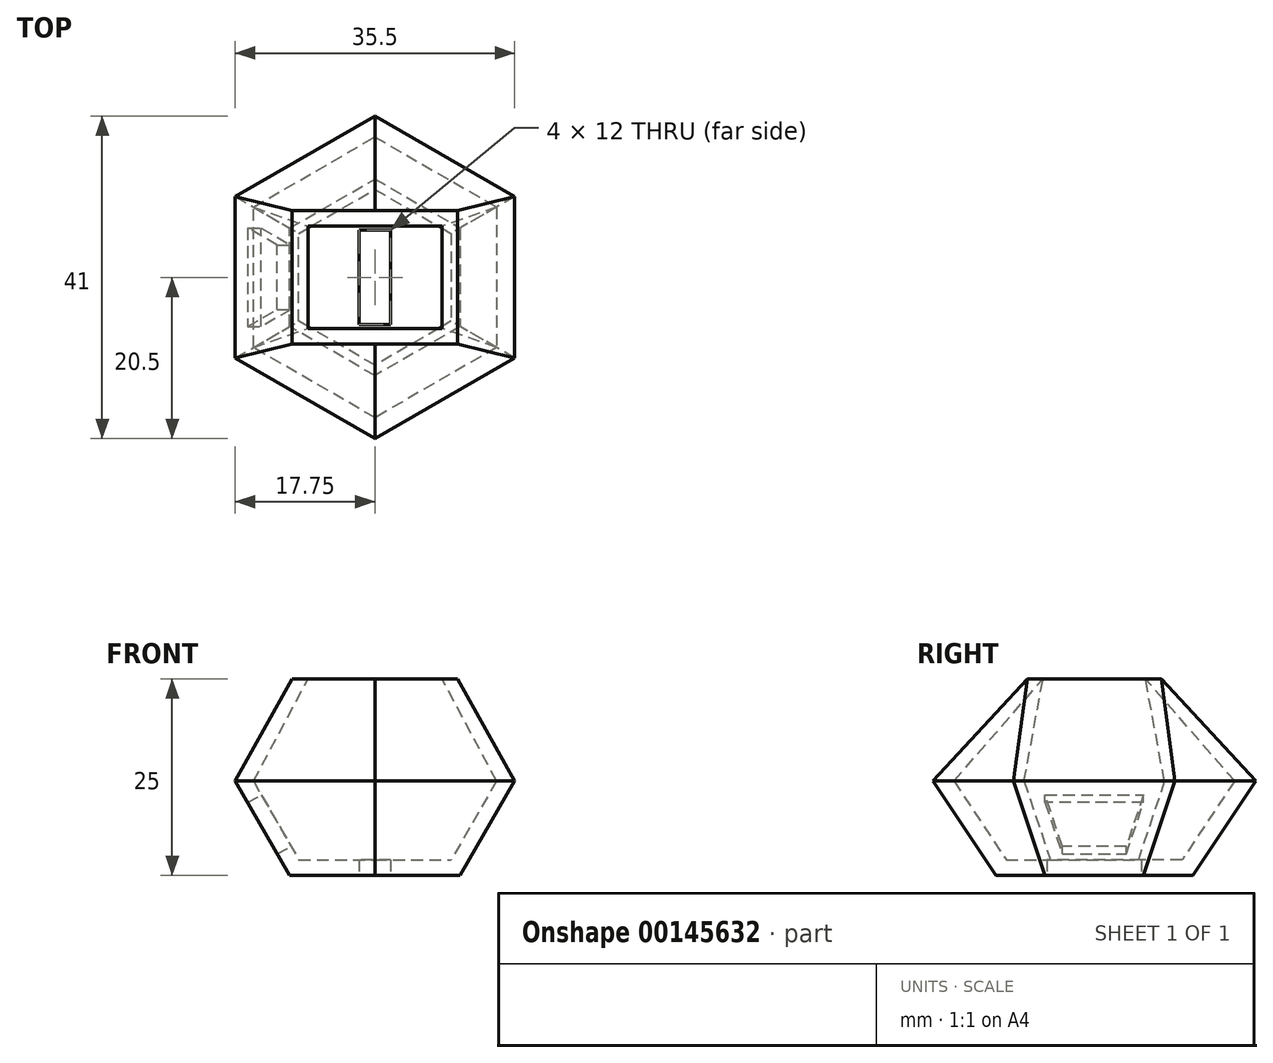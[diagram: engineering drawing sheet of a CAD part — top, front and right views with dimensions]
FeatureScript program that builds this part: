
annotation { "Feature Type Name" : "Feature", "Feature Type Description" : "" }
export const myFeature = defineFeature(function(context is Context, id is Id, definition is map)
    precondition{}
    {
        {
            assignVariable(context, id + "F0", {"name" : "tot_height", "anyValue" : 25});
        }
        {
            assignVariable(context, id + "F1", {"name" : "wall_thick", "anyValue" : 2});
        }
        {
            assignVariable(context, id + "F2", {"name" : "bottom_angle", "anyValue" : 30});
        }
        {
            assignVariable(context, id + "F3", {"name" : "bottom_height", "anyValue" : 12});
        }
        {
            var Q0;
            Q0=qCreatedBy(makeId("Top.planeOp"),FACE);
            var sketch = newSketch(context, id + "F4", { "sketchPlane" : qUnion([Q0])});
            skCircle(sketch, "E0.cCircle", {"center": v(0, 0) * mm, "radius": 12.5 * mm, "construction": true});
            skLineSegment(sketch, "E0.0", {"start": v(0, 12.5) * mm, "end": v(10.83, 6.25) * mm});
            skLineSegment(sketch, "E0.1", {"start": v(10.83, 6.25) * mm, "end": v(10.83, -6.25) * mm});
            skLineSegment(sketch, "E0.2", {"start": v(10.83, -6.25) * mm, "end": v(0, -12.5) * mm});
            skLineSegment(sketch, "E0.3", {"start": v(0, -12.5) * mm, "end": v(-10.83, -6.25) * mm});
            skLineSegment(sketch, "E0.4", {"start": v(-10.83, -6.25) * mm, "end": v(-10.83, 6.25) * mm});
            skLineSegment(sketch, "E0.5", {"start": v(-10.83, 6.25) * mm, "end": v(0, 12.5) * mm});
            skLineSegment(sketch, "E1.bottom", {"start": v(-2, -6) * mm, "end": v(2, -6) * mm});
            skLineSegment(sketch, "E1.top", {"start": v(-2, 6) * mm, "end": v(2, 6) * mm});
            skLineSegment(sketch, "E1.left", {"start": v(-2, -6) * mm, "end": v(-2, 6) * mm});
            skLineSegment(sketch, "E1.right", {"start": v(2, -6) * mm, "end": v(2, 6) * mm});
            skSolve(sketch);
        }
        {
            var Q0;
            Q0 = qSketchRegion(id + "F4", true);
            var Q1;
            Q1=makeQuery(id+"F4.imprint","IMPRINT",FACE,{"disambiguationData":[TD([[makeQuery(id+"F4.imprint","IMPRINT",EDGE,{"derivedFrom":sQuery(id+"F4.wireOp",EDGE,"E1.bottom")}),1.0]])]});
            extrude(context, id + "F5", {"entities" : qUnion([Q0, Q1]), "depth" : (getVariable(context, 'bottom_height')) * mm, "hasDraft" : true, "draftAngle" : (getVariable(context, 'bottom_angle')) * degree});
        }
        {
            var Q0;
            Q0=makeQuery(id+"F5.opExtrude","CAP_FACE",FACE,{"disambiguationData":[OSD([sQuery(id+"F4.wireOp",EDGE,"b764b78a-1ece-4713-94bb-0b7ff5981961.0"),sQuery(id+"F4.wireOp",EDGE,"b764b78a-1ece-4713-94bb-0b7ff5981961.1"),sQuery(id+"F4.wireOp",EDGE,"b764b78a-1ece-4713-94bb-0b7ff5981961.2"),sQuery(id+"F4.wireOp",EDGE,"b764b78a-1ece-4713-94bb-0b7ff5981961.3"),sQuery(id+"F4.wireOp",EDGE,"b764b78a-1ece-4713-94bb-0b7ff5981961.4"),sQuery(id+"F4.wireOp",EDGE,"b764b78a-1ece-4713-94bb-0b7ff5981961.5"),sQuery(id+"F4.wireOp",EDGE,"b764b78a-1ece-4713-94bb-0b7ff5981961.6"),sQuery(id+"F4.wireOp",EDGE,"b764b78a-1ece-4713-94bb-0b7ff5981961.7")])],"isStart":false});
            var Q1;
            Q1=makeQuery(id+"F5.opExtrude","CAP_FACE",FACE,{"disambiguationData":[OSD([sQuery(id+"F4.wireOp",EDGE,"E0.0"),sQuery(id+"F4.wireOp",EDGE,"E0.1"),sQuery(id+"F4.wireOp",EDGE,"E0.2"),sQuery(id+"F4.wireOp",EDGE,"E0.3"),sQuery(id+"F4.wireOp",EDGE,"E0.4"),sQuery(id+"F4.wireOp",EDGE,"E0.5")])],"isStart":false});
            shell(context, id + "F6", {"entities" : qUnion([Q0, Q1]), "thickness" : getVariable(context, 'wall_thick') * mm});
        }
        {
            var Q0;
            Q0=makeQuery(id+"F4.imprint","IMPRINT",FACE,{"disambiguationData":[TD([[makeQuery(id+"F4.imprint","IMPRINT",EDGE,{"derivedFrom":sQuery(id+"F4.wireOp",EDGE,"E1.bottom")}),1.0]])]});
            extrude(context, id + "F7", {"entities" : qUnion([Q0]), "operationType" : NewBodyOperationType.REMOVE, "depth" : 5 * mm});
        }
        {
            var Q0;
            Q0=makeQuery(id+"F6.opShell","OFFSET_FACE",FACE,{"disambiguationData":[OSD([sQuery(id+"F4.wireOp",EDGE,"E0.4")])]});
            var sketch = newSketch(context, id + "F8", { "sketchPlane" : qUnion([Q0])});
            skLineSegment(sketch, "E2", {"start": v(-6.26, 16.11) * mm, "end": v(6.26, 16.11) * mm});
            skLineSegment(sketch, "E3", {"start": v(6.26, 16.11) * mm, "end": v(4.08, 8.57) * mm});
            skLineSegment(sketch, "E4", {"start": v(4.08, 8.57) * mm, "end": v(-4.08, 8.57) * mm});
            skLineSegment(sketch, "E5", {"start": v(-4.08, 8.57) * mm, "end": v(-6.26, 16.11) * mm});
            skSolve(sketch);
        }
        {
            var Q0;
            Q0 = qSketchRegion(id + "F8", true);
            var Q1;
            Q1=makeQuery(id+"F6.opShell","OFFSET_FACE",FACE,{"disambiguationData":[OSD([sQuery(id+"F4.wireOp",EDGE,"b764b78a-1ece-4713-94bb-0b7ff5981961.2")])]});
            extrude(context, id + "F9", {"entities" : qUnion([Q0]), "operationType" : NewBodyOperationType.REMOVE, "oppositeDirection" : true, "endBoundEntityFace" : qUnion([Q1]), "depth" : 10 * mm});
        }
        {
            var Q0;
            Q0=makeQuery(id+"F5.opExtrude","CAP_FACE",FACE,{"disambiguationData":[OSD([sQuery(id+"F4.wireOp",EDGE,"E0.0"),sQuery(id+"F4.wireOp",EDGE,"E0.1"),sQuery(id+"F4.wireOp",EDGE,"E0.2"),sQuery(id+"F4.wireOp",EDGE,"E0.3"),sQuery(id+"F4.wireOp",EDGE,"E0.4"),sQuery(id+"F4.wireOp",EDGE,"E0.5")])],"isStart":false});
            var sketch = newSketch(context, id + "F10", { "sketchPlane" : qUnion([Q0])});
            skLineSegment(sketch, "E6.0", {"start": v(-17.75, 10.25) * mm, "end": v(0, 20.5) * mm});
            skLineSegment(sketch, "E7.0", {"start": v(0, 20.5) * mm, "end": v(17.75, 10.25) * mm});
            skLineSegment(sketch, "E8.0", {"start": v(17.75, 10.25) * mm, "end": v(17.75, -10.25) * mm});
            skLineSegment(sketch, "E9.0", {"start": v(17.75, -10.25) * mm, "end": v(0, -20.5) * mm});
            skLineSegment(sketch, "E10.0", {"start": v(0, -20.5) * mm, "end": v(-17.75, -10.25) * mm});
            skLineSegment(sketch, "E11.0", {"start": v(-17.75, -10.25) * mm, "end": v(-17.75, 10.25) * mm});
            skSolve(sketch);
        }
        {
            var Q0;
            Q0=qCreatedBy(makeId("Top.planeOp"),FACE);
            cPlane(context, id + "F11", {"entities" : qUnion([Q0]), "cplaneType" : CPlaneType.OFFSET, "offset" : (getVariable(context, 'tot_height')) * mm, "width" : 150 * mm, "height" : 150 * mm});
        }
        {
            var Q0;
            Q0=makeQuery(id+"F5.opExtrude","CAP_FACE",FACE,{"disambiguationData":[OSD([sQuery(id+"F4.wireOp",EDGE,"E0.0"),sQuery(id+"F4.wireOp",EDGE,"E0.1"),sQuery(id+"F4.wireOp",EDGE,"E0.2"),sQuery(id+"F4.wireOp",EDGE,"E0.3"),sQuery(id+"F4.wireOp",EDGE,"E0.4"),sQuery(id+"F4.wireOp",EDGE,"E0.5")])],"isStart":false});
            var sketch = newSketch(context, id + "F12", { "sketchPlane" : qUnion([Q0])});
            skLineSegment(sketch, "E12.0", {"start": v(-15.44, 8.92) * mm, "end": v(0, 17.83) * mm});
            skLineSegment(sketch, "E13.0", {"start": v(0, 17.83) * mm, "end": v(15.44, 8.92) * mm});
            skLineSegment(sketch, "E14.0", {"start": v(15.44, 8.92) * mm, "end": v(15.44, -8.92) * mm});
            skLineSegment(sketch, "E15.0", {"start": v(15.44, -8.92) * mm, "end": v(0, -17.83) * mm});
            skLineSegment(sketch, "E16.0", {"start": v(0, -17.83) * mm, "end": v(-15.44, -8.92) * mm});
            skLineSegment(sketch, "E17.0", {"start": v(-15.44, -8.92) * mm, "end": v(-15.44, 8.92) * mm});
            skSolve(sketch);
        }
        {
            var Q0;
            Q0=qCreatedBy(id+"F11.planeOp",FACE);
            var sketch = newSketch(context, id + "F13", { "sketchPlane" : qUnion([Q0])});
            skLineSegment(sketch, "E18.0", {"start": v(0, 8.5) * mm, "end": v(10.5, 8.5) * mm});
            skLineSegment(sketch, "E18.3", {"start": v(10.5, -8.5) * mm, "end": v(0, -8.5) * mm});
            skLineSegment(sketch, "E18.4", {"start": v(0, -8.5) * mm, "end": v(-10.5, -8.5) * mm});
            skLineSegment(sketch, "E18.7", {"start": v(-10.5, 8.5) * mm, "end": v(0, 8.5) * mm});
            skLineSegment(sketch, "E19", {"start": v(-10.5, 8.5) * mm, "end": v(-10.5, -8.5) * mm});
            skLineSegment(sketch, "E20", {"start": v(10.5, 8.5) * mm, "end": v(10.5, -8.5) * mm});
            skPoint(sketch, "E21", {"position": v(-10.5, 0) * mm});
            skPoint(sketch, "E22", {"position": v(10.5, 0) * mm});
            skLineSegment(sketch, "E23", {"start": v(-10.5, 0) * mm, "end": v(10.5, 0) * mm, "construction": true});
            skSolve(sketch);
        }
        {
            var Q0;
            Q0=qCreatedBy(id+"F11.planeOp",FACE);
            var sketch = newSketch(context, id + "F14", { "sketchPlane" : qUnion([Q0])});
            skLineSegment(sketch, "E24.bottom", {"start": v(8.5, 6.5) * mm, "end": v(0, 6.5) * mm});
            skLineSegment(sketch, "E24.top", {"start": v(8.5, -6.5) * mm, "end": v(0, -6.5) * mm});
            skLineSegment(sketch, "E24.left", {"start": v(8.5, 6.5) * mm, "end": v(8.5, -6.5) * mm});
            skLineSegment(sketch, "E24.right", {"start": v(-8.5, 6.5) * mm, "end": v(-8.5, -6.5) * mm});
            skPoint(sketch, "E24.middle", {"position": v(0, 0) * mm});
            skLineSegment(sketch, "E25", {"start": v(0, 6.5) * mm, "end": v(-8.5, 6.5) * mm});
            skLineSegment(sketch, "E26", {"start": v(0, -6.5) * mm, "end": v(-8.5, -6.5) * mm});
            skSolve(sketch);
        }
        {
            var Q1;
            Q1 = qSketchRegion(id + "F10", true);
            var Q2;
            Q2 = qSketchRegion(id + "F13", true);
            loft(context, id + "F15", {"operationType" : NewBodyOperationType.ADD, "sheetProfilesArray" : [{ "sheetProfileEntities" : qUnion([Q1]) }, { "sheetProfileEntities" : qUnion([Q2]) }]});
        }
        {
            var Q1;
            Q1 = qSketchRegion(id + "F12", true);
            var Q2;
            Q2 = qSketchRegion(id + "F14", true);
            loft(context, id + "F16", {"operationType" : NewBodyOperationType.REMOVE, "sheetProfilesArray" : [{ "sheetProfileEntities" : qUnion([Q1]) }, { "sheetProfileEntities" : qUnion([Q2]) }]});
        }
    });
